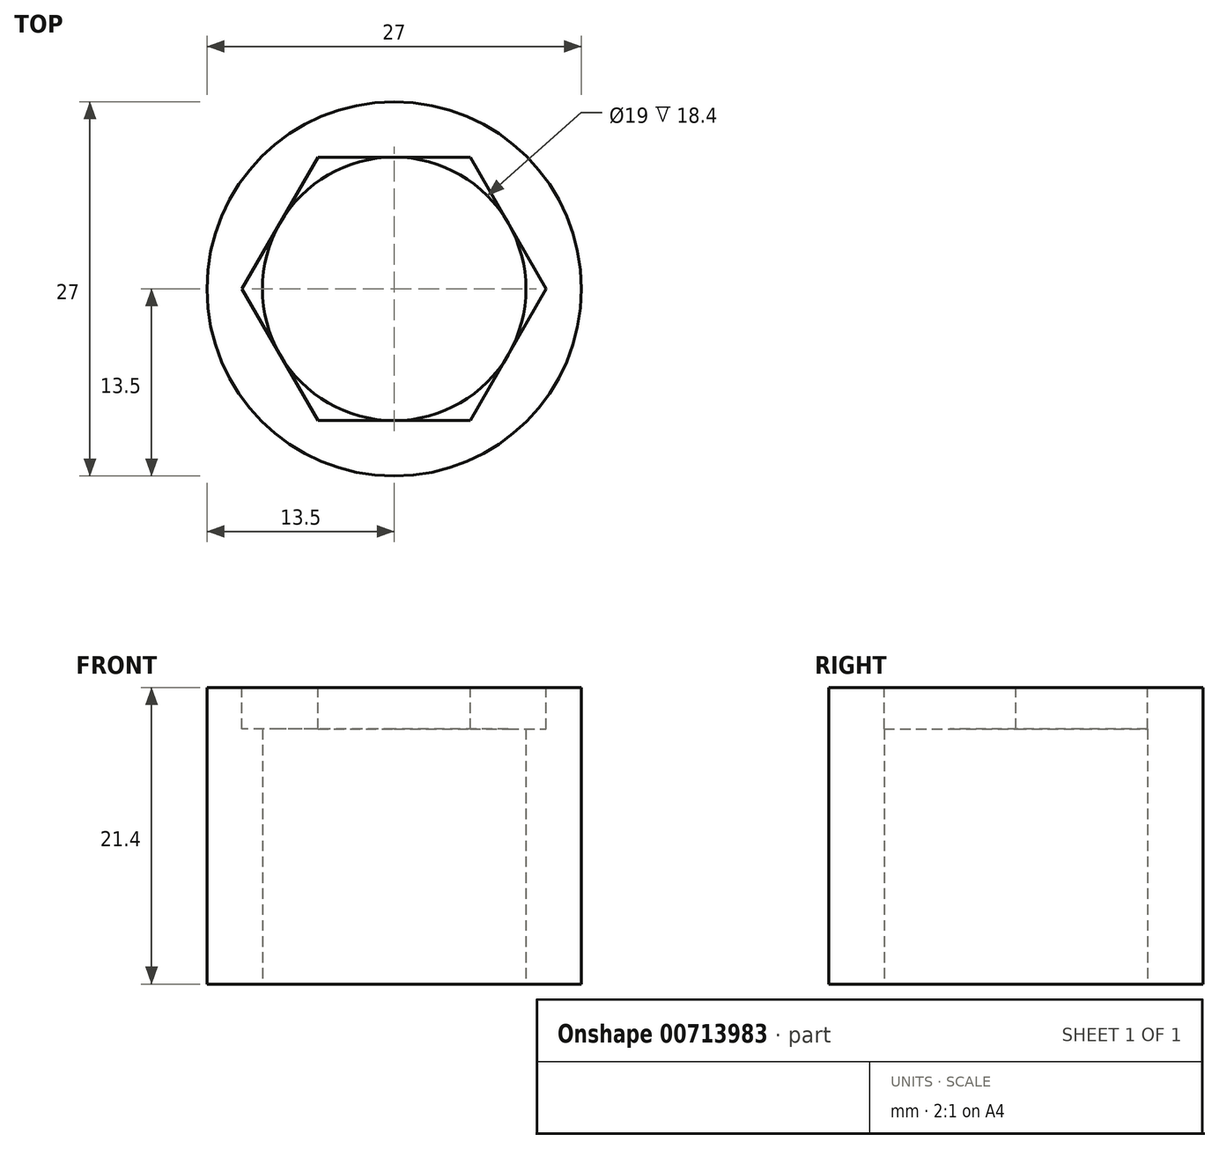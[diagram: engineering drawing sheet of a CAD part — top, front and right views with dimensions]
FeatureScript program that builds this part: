
annotation { "Feature Type Name" : "Feature", "Feature Type Description" : "" }
export const myFeature = defineFeature(function(context is Context, id is Id, definition is map)
    precondition{}
    {
        {
            var Q0;
            Q0=qCreatedBy(makeId("Top.planeOp"),FACE);
            var sketch = newSketch(context, id + "F0", { "sketchPlane" : qUnion([Q0])});
            skCircle(sketch, "E0", {"center": v(0, 0) * mm, "radius": 13.5 * mm});
            skCircle(sketch, "E1", {"center": v(0, 0) * mm, "radius": 9.5 * mm});
            skSolve(sketch);
        }
        {
            var Q0;
            Q0=makeQuery(id+"F0.imprint","IMPRINT",FACE,{"disambiguationData":[TD([[makeQuery(id+"F0.imprint","IMPRINT",EDGE,{"derivedFrom":sQuery(id+"F0.wireOp",EDGE,"E0")}),1.0]])]});
            extrude(context, id + "F1", {"entities" : qUnion([Q0]), "depth" : 21.4 * mm, "offsetDistance" : 25 * mm});
        }
        {
            var Q0;
            Q0=makeQuery(id+"F1.opExtrude","CAP_FACE",FACE,{"disambiguationData":[OSD([sQuery(id+"F0.wireOp",EDGE,"E0"),sQuery(id+"F0.wireOp",EDGE,"E1")])],"isStart":false});
            var sketch = newSketch(context, id + "F2", { "sketchPlane" : qUnion([Q0])});
            skCircle(sketch, "E2.cCircle", {"center": v(0, 0) * mm, "radius": 10.97 * mm, "construction": true});
            skLineSegment(sketch, "E2.0", {"start": v(10.97, 0) * mm, "end": v(5.48, -9.5) * mm});
            skLineSegment(sketch, "E2.1", {"start": v(5.48, -9.5) * mm, "end": v(-5.48, -9.5) * mm});
            skLineSegment(sketch, "E2.2", {"start": v(-5.48, -9.5) * mm, "end": v(-10.97, 0) * mm});
            skLineSegment(sketch, "E2.3", {"start": v(-10.97, 0) * mm, "end": v(-5.48, 9.5) * mm});
            skLineSegment(sketch, "E2.4", {"start": v(-5.48, 9.5) * mm, "end": v(5.48, 9.5) * mm});
            skLineSegment(sketch, "E2.5", {"start": v(5.48, 9.5) * mm, "end": v(10.97, 0) * mm});
            skSolve(sketch);
        }
        {
            var Q0;
            {var subQ0=sQuery(id+"F2.wireOp",EDGE,"E2.5");var subQ1=sQuery(id+"F2.wireOp",EDGE,"E2.0");var subQ2=makeQuery(id+"F2.imprint","INTERSECT",VERTEX,{"derivedFrom":[subQ1,subQ0]});Q0=makeQuery(id+"F2.imprint","IMPRINT",FACE,{"disambiguationData":[TD([[makeQuery(id+"F2.imprint","IMPRINT",EDGE,{"disambiguationData":[TD([[subQ2,-1.0]])],"derivedFrom":subQ1}),-1.0]])]});}
            var Q1;
            {var subQ0=sQuery(id+"F2.wireOp",EDGE,"E2.3");var subQ1=sQuery(id+"F2.wireOp",EDGE,"E2.2");var subQ2=makeQuery(id+"F2.imprint","INTERSECT",VERTEX,{"derivedFrom":[subQ1,subQ0]});Q1=makeQuery(id+"F2.imprint","IMPRINT",FACE,{"disambiguationData":[TD([[makeQuery(id+"F2.imprint","IMPRINT",EDGE,{"disambiguationData":[TD([[subQ2,1.0]])],"derivedFrom":subQ1}),-1.0]])]});}
            var Q2;
            {var subQ0=sQuery(id+"F2.wireOp",EDGE,"E2.2");var subQ1=sQuery(id+"F2.wireOp",EDGE,"E2.1");var subQ2=makeQuery(id+"F2.imprint","INTERSECT",VERTEX,{"derivedFrom":[subQ1,subQ0]});Q2=makeQuery(id+"F2.imprint","IMPRINT",FACE,{"disambiguationData":[TD([[makeQuery(id+"F2.imprint","IMPRINT",EDGE,{"disambiguationData":[TD([[subQ2,1.0]])],"derivedFrom":subQ1}),-1.0]])]});}
            var Q3;
            {var subQ0=sQuery(id+"F2.wireOp",EDGE,"E2.5");var subQ1=sQuery(id+"F2.wireOp",EDGE,"E2.4");var subQ2=makeQuery(id+"F2.imprint","INTERSECT",VERTEX,{"derivedFrom":[subQ1,subQ0]});Q3=makeQuery(id+"F2.imprint","IMPRINT",FACE,{"disambiguationData":[TD([[makeQuery(id+"F2.imprint","IMPRINT",EDGE,{"disambiguationData":[TD([[subQ2,1.0]])],"derivedFrom":subQ1}),-1.0]])]});}
            var Q4;
            {var subQ0=sQuery(id+"F2.wireOp",EDGE,"E2.1");var subQ1=sQuery(id+"F2.wireOp",EDGE,"E2.0");var subQ2=makeQuery(id+"F2.imprint","INTERSECT",VERTEX,{"derivedFrom":[subQ1,subQ0]});Q4=makeQuery(id+"F2.imprint","IMPRINT",FACE,{"disambiguationData":[TD([[makeQuery(id+"F2.imprint","IMPRINT",EDGE,{"disambiguationData":[TD([[subQ2,1.0]])],"derivedFrom":subQ1}),-1.0]])]});}
            var Q5;
            {var subQ0=sQuery(id+"F2.wireOp",EDGE,"E2.4");var subQ1=sQuery(id+"F2.wireOp",EDGE,"E2.3");var subQ2=makeQuery(id+"F2.imprint","INTERSECT",VERTEX,{"derivedFrom":[subQ1,subQ0]});Q5=makeQuery(id+"F2.imprint","IMPRINT",FACE,{"disambiguationData":[TD([[makeQuery(id+"F2.imprint","IMPRINT",EDGE,{"disambiguationData":[TD([[subQ2,1.0]])],"derivedFrom":subQ1}),-1.0]])]});}
            extrude(context, id + "F3", {"entities" : qUnion([Q0, Q1, Q2, Q3, Q4, Q5]), "operationType" : NewBodyOperationType.REMOVE, "oppositeDirection" : true, "depth" : 3 * mm, "offsetDistance" : 25 * mm});
        }
    });
